# Revit family: 9981 Парковый лежак «Волна» Хоббика
name_source: partatom
category: Антураж
revit_build: Autodesk Revit 2018 (Build: 20180423_1000(x64)
units: mm (PartAtom-declared; Revit-internal decimal feet)

## family parameters
Всегда вертикально = Да
Источник визуального образа = Геометрия семейства
На основе рабочей плоскости = Нет
Общий = Нет
При загрузке вырезать с полостями = Нет
Точка расчета площади = Нет

## types (4) — shared parameters
URL = https://hobbyka.ru
Артикул товара = Арт. 9981
Высота = 870 мм
Группа модели = Лежаки и шезлонги
Изготовитель = ООО «Хоббика»
Изображение типоразмера = Парковый лежак «Волна» 9981.jpg
Материал изделия = Сталь, дерево
Цвет каркаса = Сталь
Цвет отделки = Дерево
Ширина = 2362 мм

## per-type parameters (varying)
| type | Версия 140 см | Версия 200 см | Версия 70 см | Версия 90 см | Длина | Описание | Средняя опора |
| Версия 70 см | Нет | Нет | Да | Нет | 700 мм | Парковый лежак «Волна». Версия 70 см | Нет |
| Версия 90 см | Нет | Нет | Нет | Да | 900 мм | Парковый лежак «Волна». Версия 90 см | Нет |
| Версия 140 см | Да | Нет | Нет | Нет | 1400 мм | Парковый лежак «Волна». Версия 140 см | Да |
| Версия 200 см | Нет | Да | Нет | Нет | 2000 мм | Парковый лежак «Волна». Версия 200 см | Да |
